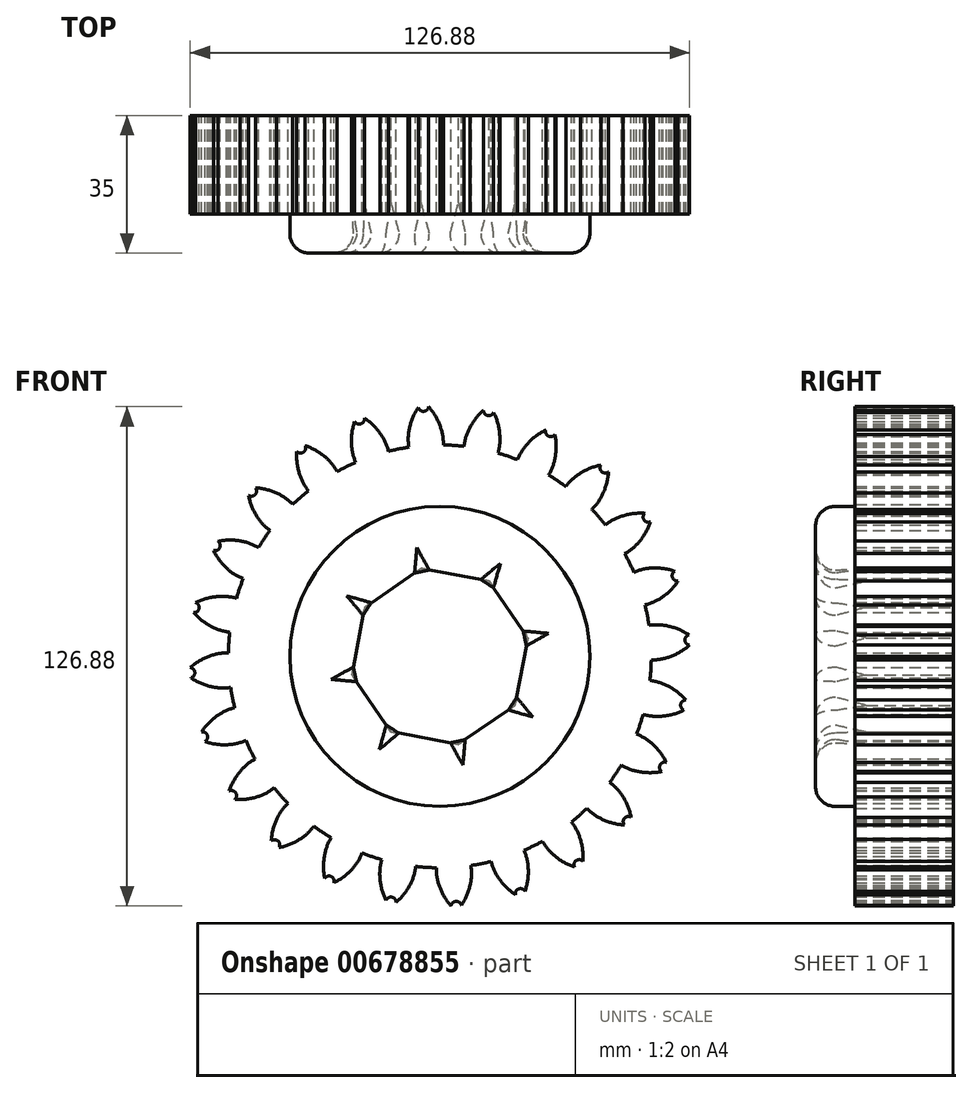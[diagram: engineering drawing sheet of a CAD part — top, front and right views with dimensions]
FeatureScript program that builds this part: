
annotation { "Feature Type Name" : "Feature", "Feature Type Description" : "" }
export const myFeature = defineFeature(function(context is Context, id is Id, definition is map)
    precondition{}
    {
        {
            var Q0;
            Q0=qCreatedBy(makeId("Front.planeOp"),FACE);
            var sketch = newSketch(context, id + "F0", { "sketchPlane" : qUnion([Q0])});
            skCircle(sketch, "E0", {"center": v(0, 0) * mm, "radius": 53.72 * mm});
            skCircle(sketch, "E1", {"center": v(0, 0) * mm, "radius": 58.67 * mm, "construction": true});
            skCircle(sketch, "E2", {"center": v(0, 0) * mm, "radius": 63.5 * mm, "construction": true});
            skLineSegment(sketch, "E3", {"start": v(0, 0) * mm, "end": v(0, 97.8) * mm, "construction": true});
            skLineSegment(sketch, "E4", {"start": v(0, 0) * mm, "end": v(-6.4, 97.8) * mm, "construction": true});
            skLineSegment(sketch, "E5", {"start": v(0, 58.67) * mm, "end": v(-71.5, 58.67) * mm, "construction": true});
            skLineSegment(sketch, "E6", {"start": v(0, 58.67) * mm, "end": v(-73, 32.1) * mm, "construction": true});
            skCircle(sketch, "E7", {"center": v(0, 0) * mm, "radius": 55.14 * mm, "construction": true});
            skCircle(sketch, "E8", {"center": v(0, 58.67) * mm, "radius": 14.6 * mm, "construction": true});
            skCircle(sketch, "E9", {"center": v(-13.72, 53.68) * mm, "radius": 14.6 * mm, "construction": true});
            skArc(sketch, "E10", {"start": v(0, 58.67) * mm, "mid": v(-1.2, 61.19) * mm, "end": v(-2.86, 63.44) * mm});
            skArc(sketch, "E11", {"start": v(0.88, 53.71) * mm, "mid": v(0.7, 56.24) * mm, "end": v(0, 58.67) * mm});
            skArc(sketch, "E12.MirrorCS", {"start": v(-7.66, 58.17) * mm, "mid": v(-6.8, 60.82) * mm, "end": v(-5.45, 63.27) * mm});
            skArc(sketch, "E13.MirrorCS", {"start": v(-7.88, 53.14) * mm, "mid": v(-8.03, 55.67) * mm, "end": v(-7.66, 58.17) * mm});
            skArc(sketch, "E14", {"start": v(-5.45, 63.27) * mm, "mid": v(-4.08, 62.24) * mm, "end": v(-2.86, 63.44) * mm});
            skCircle(sketch, "E15", {"center": v(0, 0) * mm, "radius": 38.1 * mm});
            skCircle(sketch, "E16.cCircle", {"center": v(0, 0) * mm, "radius": 21.09 * mm, "construction": true});
            skLineSegment(sketch, "E16.0", {"start": v(19.13, -12.45) * mm, "end": v(4.73, -22.33) * mm});
            skLineSegment(sketch, "E16.1", {"start": v(4.73, -22.33) * mm, "end": v(-12.45, -19.13) * mm});
            skLineSegment(sketch, "E16.2", {"start": v(-12.45, -19.13) * mm, "end": v(-22.33, -4.73) * mm});
            skLineSegment(sketch, "E16.3", {"start": v(-22.33, -4.73) * mm, "end": v(-19.13, 12.45) * mm});
            skLineSegment(sketch, "E16.4", {"start": v(-19.13, 12.45) * mm, "end": v(-4.73, 22.33) * mm});
            skLineSegment(sketch, "E16.5", {"start": v(-4.73, 22.33) * mm, "end": v(12.45, 19.13) * mm});
            skLineSegment(sketch, "E16.6", {"start": v(12.45, 19.13) * mm, "end": v(22.33, 4.73) * mm});
            skLineSegment(sketch, "E16.7", {"start": v(22.33, 4.73) * mm, "end": v(19.13, -12.45) * mm});
            skPoint(sketch, "E16.0.midPoint", {"position": v(11.93, -17.39) * mm});
            skSolve(sketch);
        }
        {
            var Q0;
            {var subQ0=sQuery(id+"F0.wireOp",EDGE,"E0");var subQ1=makeQuery(id+"F0.imprint","INTERSECT",VERTEX,{"derivedFrom":[subQ0,sQuery(id+"F0.wireOp",EDGE,"E11")]});Q0=makeQuery(id+"F0.imprint","IMPRINT",FACE,{"disambiguationData":[TD([[makeQuery(id+"F0.imprint","IMPRINT",EDGE,{"disambiguationData":[TD([[subQ1,-1.0]])],"derivedFrom":subQ0}),1.0]])]});}
            var Q1;
            Q1=makeQuery(id+"F0.imprint","IMPRINT",FACE,{"disambiguationData":[TD([[makeQuery(id+"F0.imprint","IMPRINT",EDGE,{"derivedFrom":sQuery(id+"F0.wireOp",EDGE,"E10")}),1.0]])]});
            extrude(context, id + "F1", {"entities" : qUnion([Q0, Q1]), "depth" : 25 * mm, "offsetDistance" : 25 * mm});
        }
        {
            var Q0;
            Q0=makeQuery(id+"F1.opExtrude","SWEPT_BODY",BODY,{"disambiguationData":[OSD([sQuery(id+"F0.wireOp",EDGE,"E0"),sQuery(id+"F0.wireOp",EDGE,"E10"),sQuery(id+"F0.wireOp",EDGE,"E11"),sQuery(id+"F0.wireOp",EDGE,"E12.MirrorCS"),sQuery(id+"F0.wireOp",EDGE,"E13.MirrorCS"),sQuery(id+"F0.wireOp",EDGE,"E14")])]});
            var Q1;
            Q1=makeQuery(id+"F1.opExtrude","SWEPT_FACE",FACE,{"disambiguationData":[OSD([sQuery(id+"F0.wireOp",EDGE,"E0")])]});
            circularPattern(context, id + "F2", {"entities" : qUnion([Q0]), "axis" : qUnion([Q1]), "angle" : 360 * degree, "instanceCount" : 24, "equalSpace" : true});
        }
        {
            var Q0;
            Q0=makeQuery(id+"F0.imprint","IMPRINT",FACE,{"disambiguationData":[TD([[makeQuery(id+"F0.imprint","IMPRINT",EDGE,{"derivedFrom":sQuery(id+"F0.wireOp",EDGE,"E15")}),1.0]])]});
            extrude(context, id + "F3", {"entities" : qUnion([Q0]), "operationType" : NewBodyOperationType.ADD, "depth" : 35 * mm, "offsetDistance" : 25 * mm});
        }
        {
            var Q0;
            Q0=makeQuery(id+"F3.opExtrude","CAP_FACE",FACE,{"disambiguationData":[OSD([sQuery(id+"F0.wireOp",EDGE,"E15"),sQuery(id+"F0.wireOp",EDGE,"E16.0"),sQuery(id+"F0.wireOp",EDGE,"E16.1"),sQuery(id+"F0.wireOp",EDGE,"E16.2"),sQuery(id+"F0.wireOp",EDGE,"E16.3"),sQuery(id+"F0.wireOp",EDGE,"E16.4"),sQuery(id+"F0.wireOp",EDGE,"E16.5"),sQuery(id+"F0.wireOp",EDGE,"E16.6"),sQuery(id+"F0.wireOp",EDGE,"E16.7")])],"isStart":false});
            fillet(context, id + "F4", {"entities" : qUnion([Q0]), "radius" : 5 * mm, "tangentPropagation" : true, "allowEdgeOverflow" : false});
        }
        {
            var Q0;
            Q0=makeQuery(id+"F3.opExtrude","CAP_FACE",FACE,{"disambiguationData":[OSD([sQuery(id+"F0.wireOp",EDGE,"E15"),sQuery(id+"F0.wireOp",EDGE,"E16.0"),sQuery(id+"F0.wireOp",EDGE,"E16.1"),sQuery(id+"F0.wireOp",EDGE,"E16.2"),sQuery(id+"F0.wireOp",EDGE,"E16.3"),sQuery(id+"F0.wireOp",EDGE,"E16.4"),sQuery(id+"F0.wireOp",EDGE,"E16.5"),sQuery(id+"F0.wireOp",EDGE,"E16.6"),sQuery(id+"F0.wireOp",EDGE,"E16.7")])],"isStart":false});
            var Q1;
            Q1=makeQuery(id+"F4.opFillet","BLEND_FACE",FACE,{"disambiguationData":[OSD([sQuery(id+"F0.wireOp",EDGE,"E15")])]});
            var Q2;
            Q2=makeQuery(id+"F4.opFillet","BLEND_FACE",FACE,{"disambiguationData":[OSD([sQuery(id+"F0.wireOp",EDGE,"E16.3")])]});
            var Q3;
            Q3=makeQuery(id+"F4.opFillet","BLEND_FACE",FACE,{"disambiguationData":[OSD([sQuery(id+"F0.wireOp",EDGE,"E16.4")])]});
            var Q4;
            Q4=makeQuery(id+"F4.opFillet","BLEND_FACE",FACE,{"disambiguationData":[OSD([sQuery(id+"F0.wireOp",EDGE,"E16.5")])]});
            var Q5;
            Q5=makeQuery(id+"F4.opFillet","BLEND_FACE",FACE,{"disambiguationData":[OSD([sQuery(id+"F0.wireOp",EDGE,"E16.6")])]});
            var Q6;
            Q6=makeQuery(id+"F4.opFillet","BLEND_FACE",FACE,{"disambiguationData":[OSD([sQuery(id+"F0.wireOp",EDGE,"E16.7")])]});
            var Q7;
            Q7=makeQuery(id+"F4.opFillet","BLEND_FACE",FACE,{"disambiguationData":[OSD([sQuery(id+"F0.wireOp",EDGE,"E16.0")])]});
            var Q8;
            Q8=makeQuery(id+"F4.opFillet","BLEND_FACE",FACE,{"disambiguationData":[OSD([sQuery(id+"F0.wireOp",EDGE,"E16.1")])]});
            var Q9;
            Q9=makeQuery(id+"F4.opFillet","BLEND_FACE",FACE,{"disambiguationData":[OSD([sQuery(id+"F0.wireOp",EDGE,"E16.2")])]});
            chamfer(context, id + "F5", {"entities" : qUnion([Q0, Q1, Q2, Q3, Q4, Q5, Q6, Q7, Q8, Q9]), "width" : 5 * mm, "tangentPropagation" : true});
        }
    });
